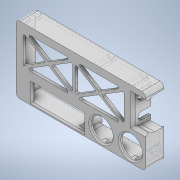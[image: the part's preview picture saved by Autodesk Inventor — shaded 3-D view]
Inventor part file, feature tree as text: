
AUTODESK INVENTOR PART (.ipt)
format: ipt  version: 2021 (Build 250183000, 183)  size: 669,696 bytes
history: native  units: mm
features: sketch x28, extrude x25, fillet x8, chamfer x8, hole x3
ambient origin geometry x8: Origin, YZ Plane, XZ Plane, XY Plane, X Axis, Y Axis, Z Axis, Center Point
bodies: Solid1 (feature_tree)
feature tree (72):
  extrude  "Extrusion1"  Depth=52.0mm
  extrude  "Extrusion2"  Depth=50.0mm
  extrude  "Extrusion3"  Depth=2.0mm
  extrude  "Extrusion4"  Depth=2.0mm
  fillet  "Fillet1"  Radius=2.0mm
  chamfer  "Chamfer1"  Distance=12.0mm
  extrude  "Extrusion5"  Depth=10.4mm
  extrude  "Extrusion6"  Depth=10.4mm
  extrude  "Extrusion7"  Depth=17.0mm
  extrude  "Extrusion8"  Depth=40.0mm
  extrude  "Extrusion9"  Depth=2.0mm
  chamfer  "Chamfer2"  Distance=2.0mm
  extrude  "Extrusion10"  Depth=1.0mm TaperAngle=45.0deg
  fillet  "Fillet3"  Radius=88.0mm
  chamfer  "Chamfer3"  Distance=20.0mm
  extrude  "Extrusion11"  Depth=2.0mm TaperAngle=0.0deg
  extrude  "Extrusion12"  Depth=11.0mm
  hole  "Hole1"  [1 undecoded]
  extrude  "Extrusion13"  TaperAngle=0.0deg  [1 undecoded]
  hole  "Hole2"  [1 undecoded]
  extrude  "Extrusion14"  Depth=12.0mm
  extrude  "Extrusion15"  Depth=2.0mm TaperAngle=45.0deg
  extrude  "Extrusion16"  Depth=40.0mm
  extrude  "Extrusion17"  Depth=6.0mm
  fillet  "Fillet4"  Radius=14.0mm
  extrude  "Extrusion21"  Depth=2.0mm TaperAngle=0.0deg
  chamfer  "Chamfer6"  Distance=1.0mm Angle=45.0deg
  extrude  "Extrusion22"  Depth=3.0mm
  extrude  "Extrusion23"  Depth=49.0mm
  extrude  "Extrusion24"  Depth=49.0mm
  chamfer  "Chamfer8"  Distance=2.0mm
  chamfer  "Chamfer9"  Distance=2.0mm
  fillet  "Fillet5"  Radius=5.0mm
  extrude  "Extrusion25"  Depth=5.0mm
  fillet  "Fillet6"  Radius=5.0mm
  chamfer  "Chamfer11"  Distance=12.0mm
  extrude  "Extrusion26"  Depth=3.0mm
  hole  "Hole3"  [1 undecoded]
  chamfer  "Chamfer12"  Distance=2.0mm
  fillet  "Fillet7"  Radius=5.0mm
  extrude  "Extrusion27"  Depth=12.0mm TaperAngle=0.0deg
  extrude  "Extrusion28"  Depth=1.0mm
  fillet  "Fillet8"  Radius=97.0mm
  fillet  "Fillet9"  Radius=4.2mm
  sketch  "Sketch1"  dims[d0=100.0mm d1=52.0mm]
  sketch  "Sketch2"  dims[d2=26.0mm d3=50.0mm]
  sketch  "Sketch3"  dims[d4=2.0mm d5=0.0mm d6=2.0mm]
  sketch  "Sketch4"  dims[d7=2.0mm d8=2.0mm d9=2.0mm d10=12.0mm d11=0.0mm]
  sketch  "Sketch5"  dims[d12=65.5mm d13=10.4mm]
  sketch  "Sketch6"  dims[d14=88.25mm d15=10.4mm]
  sketch  "Sketch7"  dims[d16=17.0mm d17=17.0mm]
  sketch  "Sketch8"  dims[d18=2.0mm d19=0.0mm d20=40.0mm]
  sketch  "Sketch9"  dims[d21=13.0mm d22=2.0mm]
  sketch  "Sketch10"  dims[d23=12.0mm d24=2.0mm d25=0.0mm]
  sketch  "Sketch11"  dims[d26=3.0mm d27=1.0mm d28=2.0mm d29=45.0deg d30=88.0mm]
  sketch  "Sketch12"  dims[d31=29.0mm]
  sketch  "Sketch13"  dims[d32=23.0mm d33=20.0mm d34=0.0mm]
  sketch  "Sketch14"  dims[d35=2.0mm d36=0.0mm d37=2.0mm d38=0.0mm]
  sketch  "Sketch15"  dims[d39=11.0mm d40=11.0mm]
  sketch  "Sketch16"  dims[d41=42.0mm d42=29.0mm]
  sketch  "Sketch17"  dims[d43=7.0mm d44=0.0mm]
  sketch  "Sketch18"  dims[d45=5.8mm d46=5.8mm]
  sketch  "Sketch19"  dims[d47=2.0mm d48=0.0mm d49=12.0mm]
  sketch  "Sketch23"  dims[d50=20.0mm d51=0.0mm d52=2.0mm d53=2.0mm d54=45.0deg]
  sketch  "Sketch24"  dims[d56=30.0mm d57=40.0mm]
  sketch  "Sketch25"  dims[d58=3.5mm d59=6.0mm d60=14.0mm]
  sketch  "Sketch27"  dims[d61=16.0mm d62=2.0mm d63=0.0mm]
  sketch  "Sketch28"  dims[d64=1.0mm d65=1.0mm d66=2.0mm d67=45.0deg]
  sketch  "Sketch29"  dims[d68=3.0mm d69=49.0mm]
  sketch  "Sketch30"  dims[d70=60.0mm d71=49.0mm]
  sketch  "Sketch31"  dims[d72=85.0mm d73=49.0mm]
  sketch  "Sketch32"  dims[d74=2.0mm d75=2.0mm d76=2.0mm d77=5.0mm d78=5.0mm d79=5.0mm d80=12.0mm d81=0.0mm d82=3.0mm d83=3.0mm d84=2.0mm d85=5.0mm d86=12.0mm d87=0.0mm d88=2.0mm d89=6.0mm d90=4.0mm d91=2.0mm d92=90.0deg d93=6.5mm d94=20.594885mm d95=8.0mm d96=97.0mm d97=4.2mm d98=12.0mm d99=0.0mm d100=2.0mm d101=6.0mm d102=4.0mm d103=2.0mm d104=90.0deg d105=6.5mm d106=20.594885mm d107=7.0mm d108=5.8mm d109=5.8mm d110=2.0mm d111=11.0mm d112=0.0mm d113=1.0mm d114=0.0mm d115=2.0mm d116=10.0mm d117=0.0mm d118=0.0mm d119=1.0mm d120=0.0mm d160=2.0mm d161=5.0mm d162=1.0mm d163=1.0mm d164=11.0mm d165=0.0mm d166=4.0mm d167=2.0mm d168=45.0deg d169=7.0mm d170=14.0mm d171=0.0mm d172=12.0mm d173=10.0mm d174=0.0mm d182=4.0mm d183=0.0mm d184=0.0mm d185=10.0mm d186=0.0mm d187=2.0mm d188=2.0mm d189=45.0deg d190=2.0mm d191=2.0mm d192=45.0deg d193=3.0mm d194=17.0mm d195=17.0mm d196=5.0mm d197=0.0mm d201=2.0mm d202=1.5mm d203=2.0mm d204=45.0deg d205=50.0mm d206=3.0mm d207=5.0mm d208=7.5mm d209=0.0mm d210=2.0mm d211=6.0mm d212=4.0mm d213=2.0mm d214=90.0deg d215=6.5mm d216=20.594885mm d217=3.49mm d218=2.0mm d219=45.0deg d220=2.0mm d221=5.5mm d222=5.5mm d223=6.5mm d224=24.0mm d225=2.0mm d226=0.0mm d227=2.0mm d228=2.0mm d229=2.0mm d230=2.0mm d231=2.0mm d232=2.0mm d233=0.0mm d234=1.0mm d235=1.0mm]
note: 4 required parameter values undecoded (feature->parameter linkage not recoverable at this tier; creation-order binding heuristic only, values carry confidence <= 0.55)
